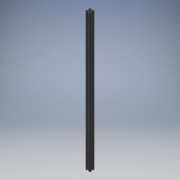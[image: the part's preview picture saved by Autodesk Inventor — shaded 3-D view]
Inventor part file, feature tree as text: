
AUTODESK INVENTOR PART (.ipt)
format: ipt  version: 2018 (Build 220112000, 112)  size: 249,856 bytes
history: native  units: mm
features: other x42, extrude x1, sketch x1
ambient origin geometry x8: Origin, YZ Plane, XZ Plane, XY Plane, X Axis, Y Axis, Z Axis, Center Point
bodies: Solid1 (feature_tree)
feature tree (44):
  extrude  "Extrusion1"  TaperAngle=0.0deg  [1 undecoded]
  other  "end_XY"
  other  "end_YZ"
  other  "end_ZX"
  other  "end_X"
  other  "end_Y"
  other  "end_Z"
  other  "end_Center"
  other  "side_1a_XY"
  other  "side_1a_YZ"
  other  "side_1a_ZX"
  other  "side_1a_X"
  other  "side_1a_Y"
  other  "side_1a_Z"
  other  "side_1a_Center"
  other  "side_2b_XY"
  other  "side_2b_YZ"
  other  "side_2b_ZX"
  other  "side_2b_X"
  other  "side_2b_Y"
  other  "side_2b_Z"
  other  "side_2b_Center"
  other  "side_3c_XY"
  other  "side_3c_YZ"
  other  "side_3c_ZX"
  other  "side_3c_X"
  other  "side_3c_Y"
  other  "side_3c_Z"
  other  "side_3c_Center"
  other  "side_4d_XY"
  other  "side_4d_YZ"
  other  "side_4d_ZX"
  other  "side_4d_X"
  other  "side_4d_Y"
  other  "side_4d_Z"
  other  "side_4d_Center"
  other  "start_XY"
  other  "start_YZ"
  other  "start_ZX"
  other  "start_X"
  other  "start_Y"
  other  "start_Z"
  other  "start_Center"
  sketch  "Skizze_1"  dims[d0=910.0mm d1=0.0mm d2=0.0mm d3=0.0mm]
note: 1 required parameter value undecoded (feature->parameter linkage not recoverable at this tier; creation-order binding heuristic only, values carry confidence <= 0.55)
